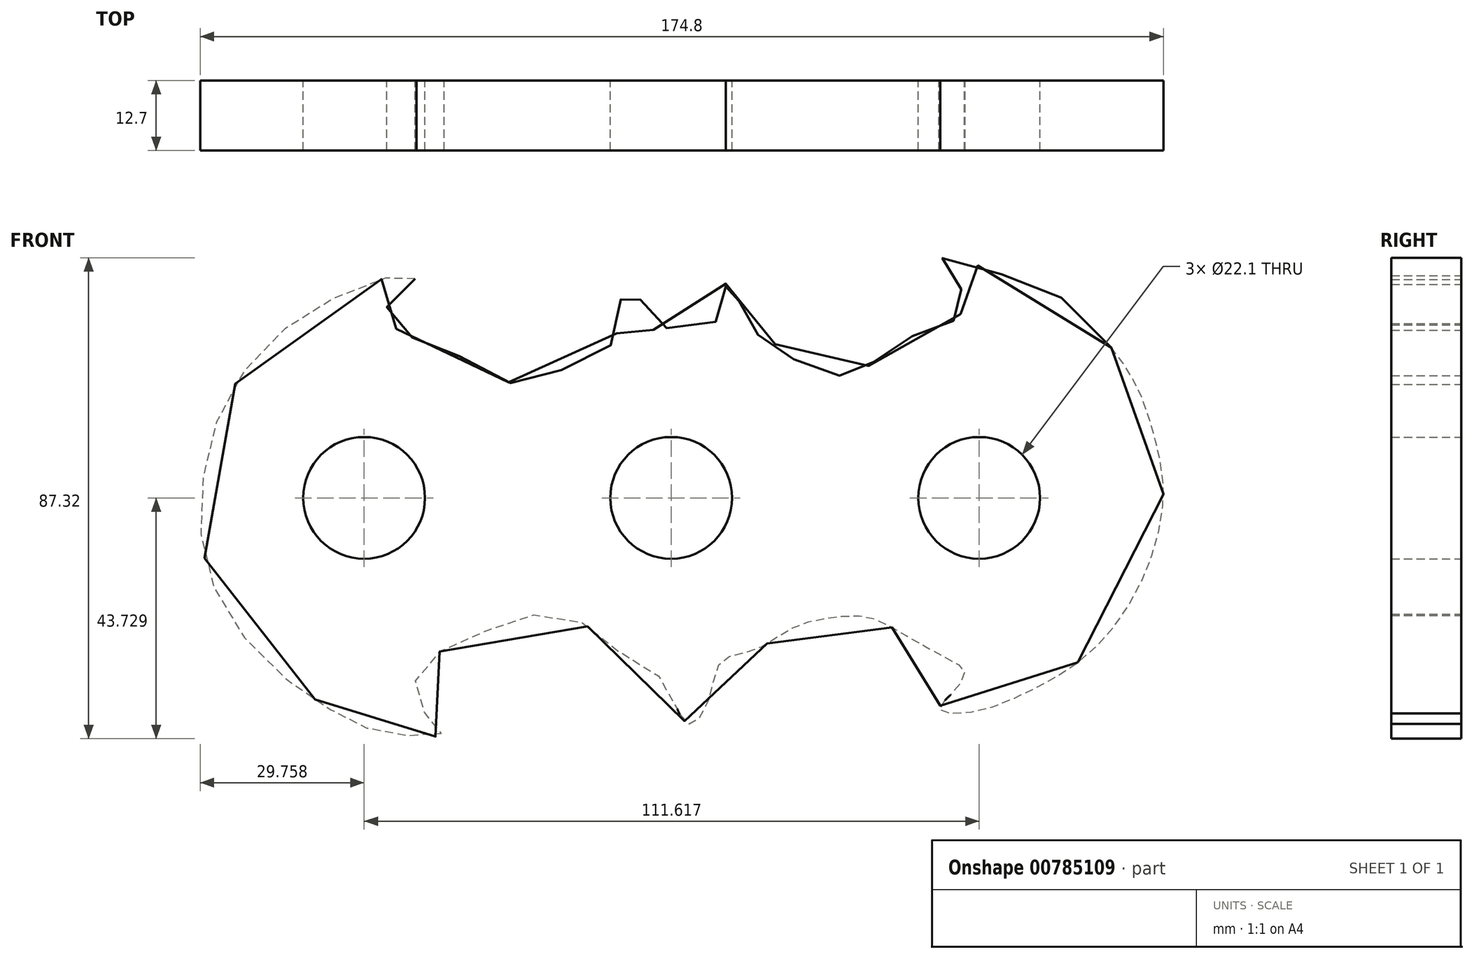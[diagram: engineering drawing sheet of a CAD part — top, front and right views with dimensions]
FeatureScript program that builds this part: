
annotation { "Feature Type Name" : "Feature", "Feature Type Description" : "" }
export const myFeature = defineFeature(function(context is Context, id is Id, definition is map)
    precondition{}
    {
        {
            var Q0;
            Q0=qCreatedBy(makeId("Front.planeOp"),FACE);
            var sketch = newSketch(context, id + "F0", { "sketchPlane" : qUnion([Q0])});
            skFitSpline(sketch, "E0", {"points": [v(79.9, 22.26) * mm, v(71.98, 30.6) * mm, v(63.23, 34.35) * mm, v(54.06, 37.68) * mm, v(48.85, 38.3) * mm, v(51.14, 35.18) * mm, v(53.02, 32.05) * mm, v(53.22, 29.76) * mm, v(51.14, 27.05) * mm, v(47.8, 25.8) * mm, v(42.8, 23.92) * mm, v(38.63, 21.21) * mm, v(35.1, 18.5) * mm, v(32.38, 17.46) * mm, v(29.46, 17.25) * mm, v(23.83, 19.13) * mm, v(19.67, 22.26) * mm, v(16.33, 24.34) * mm, v(13.41, 26) * mm, v(12.37, 29.97) * mm, v(11.54, 34.35) * mm, v(10.08, 34.35) * mm, v(9.87, 32.47) * mm, v(8.62, 29.34) * mm, v(7.79, 26.63) * mm, v(2.57, 26.63) * mm, v(-3.47, 25.6) * mm, v(-5.35, 29.97) * mm, v(-6.8, 33.72) * mm, v(-8.47, 32.68) * mm, v(-9.72, 26.84) * mm, v(-10.77, 22.88) * mm, v(-16.4, 20.17) * mm, v(-22.85, 16.63) * mm, v(-28.9, 15.8) * mm, v(-35.78, 19.13) * mm, v(-42.03, 22.47) * mm, v(-47.03, 24.13) * mm, v(-50.37, 26.22) * mm, v(-51.62, 29.97) * mm, v(-50.37, 33.1) * mm, v(-46.2, 34.97) * mm, v(-50.16, 35.18) * mm, v(-61.62, 31.01) * mm, v(-72.67, 23.5) * mm, v(-81, 12.25) * mm, v(-84.76, 0) * mm, v(-85.18, -13.18) * mm, v(-81.22, -24.85) * mm, v(-71.84, -36.31) * mm, v(-62.25, -43.2) * mm, v(-56.2, -46.53) * mm, v(-49.12, -47.82) * mm, v(-44.12, -48.7) * mm, v(-41.2, -46.93) * mm, v(-44.74, -43.99) * mm, v(-46.4, -40.15) * mm, v(-45.16, -35.14) * mm, v(-36.82, -30.72) * mm, v(-28.07, -26.89) * mm, v(-17.64, -26.89) * mm, v(-11.4, -31.6) * mm, v(-2.85, -36.91) * mm, v(0, -40.74) * mm, v(3.2, -46.05) * mm, v(6.74, -41.92) * mm, v(9.24, -34.55) * mm, v(14.66, -32.78) * mm, v(21.96, -28.66) * mm, v(28.21, -26.89) * mm, v(35.5, -26.6) * mm, v(41.76, -29.54) * mm, v(51.35, -34.85) * mm, v(53.22, -36.62) * mm, v(51.35, -40.15) * mm, v(48.64, -43.4) * mm, v(54.06, -43.99) * mm, v(64.9, -40.15) * mm, v(76.36, -32.78) * mm, v(85.53, -19.81) * mm, v(89.28, -5.66) * mm, v(88.03, 4.95) * mm, v(84.49, 15.26) * mm, v(79.9, 22.26) * mm]});
            skCircle(sketch, "E1", {"center": v(-55.71, -5.01) * mm, "radius": 11.05 * mm});
            skCircle(sketch, "E2", {"center": v(0, -5.01) * mm, "radius": 11.05 * mm});
            skCircle(sketch, "E3", {"center": v(55.9, -5.01) * mm, "radius": 11.05 * mm});
            skSolve(sketch);
        }
        {
            var Q0;
            Q0=makeQuery(id+"F0.imprint","IMPRINT",FACE,{"disambiguationData":[TD([[makeQuery(id+"F0.imprint","IMPRINT",EDGE,{"derivedFrom":sQuery(id+"F0.wireOp",EDGE,"E0")}),1.0]])]});
            extrude(context, id + "F1", {"entities" : qUnion([Q0]), "depth" : 12.7 * mm, "offsetDistance" : 25.4 * mm});
        }
    });
